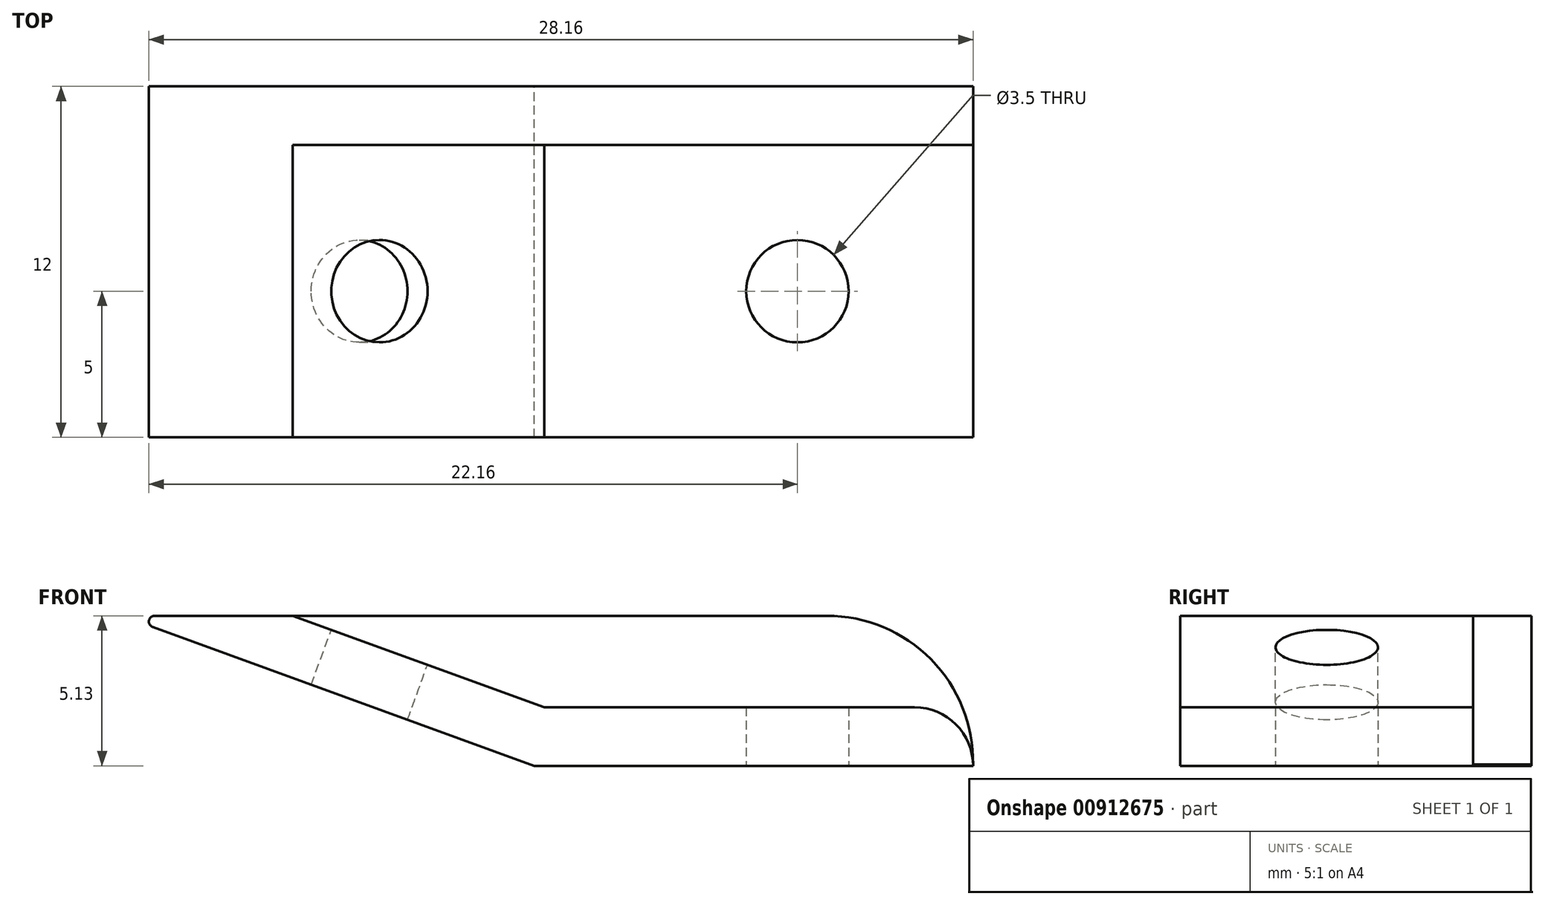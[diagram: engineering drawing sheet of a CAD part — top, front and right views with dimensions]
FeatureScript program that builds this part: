
annotation { "Feature Type Name" : "Feature", "Feature Type Description" : "" }
export const myFeature = defineFeature(function(context is Context, id is Id, definition is map)
    precondition{}
    {
        {
            var Q0;
            Q0=qCreatedBy(makeId("Front.planeOp"),FACE);
            var sketch = newSketch(context, id + "F0", { "sketchPlane" : qUnion([Q0])});
            skLineSegment(sketch, "E0", {"start": v(0, 0) * mm, "end": v(-15, 0) * mm});
            skLineSegment(sketch, "E1", {"start": v(-15, 0) * mm, "end": v(-29.1, 5.13) * mm});
            skLineSegment(sketch, "E2", {"start": v(-29.1, 5.13) * mm, "end": v(-5, 5.13) * mm});
            skLineSegment(sketch, "E3", {"start": v(0, 0.13) * mm, "end": v(0, 0) * mm});
            skPoint(sketch, "E4.visualSharp", {"position": v(0, 5.13) * mm});
            skArc(sketch, "E4.filletArc", {"start": v(0, 0.13) * mm, "mid": v(-1.46, 3.67) * mm, "end": v(-5, 5.13) * mm});
            skSolve(sketch);
        }
        {
            var Q0;
            Q0 = qSketchRegion(id + "F0", true);
            extrude(context, id + "F1", {"entities" : qUnion([Q0]), "depth" : 2 * mm, "offsetDistance" : 25 * mm});
        }
        {
            var Q0;
            Q0=makeQuery(id+"F1.opExtrude","CAP_FACE",FACE,{"disambiguationData":[OSD([sQuery(id+"F0.wireOp",EDGE,"E0"),sQuery(id+"F0.wireOp",EDGE,"E1"),sQuery(id+"F0.wireOp",EDGE,"E2"),sQuery(id+"F0.wireOp",EDGE,"E3"),sQuery(id+"F0.wireOp",EDGE,"E4.filletArc")])],"isStart":false});
            var sketch = newSketch(context, id + "F2", { "sketchPlane" : qUnion([Q0])});
            skLineSegment(sketch, "E5", {"start": v(-29.1, 5.13) * mm, "end": v(-15, 0) * mm});
            skLineSegment(sketch, "E6", {"start": v(-15, 0) * mm, "end": v(0, 0) * mm});
            skLineSegment(sketch, "E7.0", {"start": v(-14.65, 2) * mm, "end": v(0, 2) * mm});
            skLineSegment(sketch, "E7.1", {"start": v(-23.25, 5.13) * mm, "end": v(-14.65, 2) * mm});
            skLineSegment(sketch, "E8", {"start": v(-29.1, 5.13) * mm, "end": v(-23.25, 5.13) * mm});
            skLineSegment(sketch, "E9", {"start": v(0, 2) * mm, "end": v(0, 0) * mm});
            skSolve(sketch);
        }
        {
            var Q0;
            Q0 = qSketchRegion(id + "F2", true);
            extrude(context, id + "F3", {"entities" : qUnion([Q0]), "operationType" : NewBodyOperationType.ADD, "depth" : 10 * mm, "offsetDistance" : 25 * mm});
        }
        {
            var Q0;
            Q0=makeQuery(id+"F3.boolean.opBoolean","MERGE",EDGE,{"derivedFrom":[makeQuery(id+"F1.opExtrude","SWEPT_EDGE",EDGE,{"disambiguationData":[OSD([sQuery(id+"F0.wireOp",EDGE,"E1"),sQuery(id+"F0.wireOp",EDGE,"E2")])]}),makeQuery(id+"F3.opExtrude","SWEPT_EDGE",EDGE,{"disambiguationData":[OSD([sQuery(id+"F2.wireOp",EDGE,"E5"),sQuery(id+"F2.wireOp",EDGE,"E8")])]})]});
            fillet(context, id + "F4", {"entities" : qUnion([Q0]), "radius" : 0.2 * mm, "tangentPropagation" : true, "allowEdgeOverflow" : false});
        }
        {
            var Q0;
            Q0=makeQuery(id+"F3.opExtrude","SWEPT_FACE",FACE,{"disambiguationData":[OSD([sQuery(id+"F2.wireOp",EDGE,"E7.1")])]});
            var sketch = newSketch(context, id + "F5", { "sketchPlane" : qUnion([Q0])});
            skCircle(sketch, "E10", {"center": v(-20.45, -7) * mm, "radius": 1.75 * mm});
            skSolve(sketch);
        }
        {
            var Q0;
            Q0 = qSketchRegion(id + "F5", true);
            extrude(context, id + "F6", {"entities" : qUnion([Q0]), "operationType" : NewBodyOperationType.REMOVE, "endBound" : BoundingType.UP_TO_NEXT, "oppositeDirection" : true, "depth" : 25 * mm, "offsetDistance" : 25 * mm});
        }
        {
            var Q0;
            Q0=makeQuery(id+"F3.boolean.opBoolean","MERGE",FACE,{"derivedFrom":[makeQuery(id+"F1.opExtrude","SWEPT_FACE",FACE,{"disambiguationData":[OSD([sQuery(id+"F0.wireOp",EDGE,"E0")])]}),makeQuery(id+"F3.opExtrude","SWEPT_FACE",FACE,{"disambiguationData":[OSD([sQuery(id+"F2.wireOp",EDGE,"E6")])]})]});
            var sketch = newSketch(context, id + "F7", { "sketchPlane" : qUnion([Q0])});
            skCircle(sketch, "E11", {"center": v(-6, 7) * mm, "radius": 1.75 * mm});
            skSolve(sketch);
        }
        {
            var Q0;
            Q0 = qSketchRegion(id + "F7", true);
            extrude(context, id + "F8", {"entities" : qUnion([Q0]), "operationType" : NewBodyOperationType.REMOVE, "endBound" : BoundingType.UP_TO_NEXT, "oppositeDirection" : true, "depth" : 25 * mm, "offsetDistance" : 25 * mm});
        }
        {
            var Q0;
            Q0=makeQuery(id+"F3.opExtrude","SWEPT_EDGE",EDGE,{"disambiguationData":[OSD([sQuery(id+"F2.wireOp",EDGE,"E7.0"),sQuery(id+"F2.wireOp",EDGE,"E9")])]});
            fillet(context, id + "F9", {"entities" : qUnion([Q0]), "radius" : 2 * mm, "tangentPropagation" : true, "allowEdgeOverflow" : false});
        }
    });
